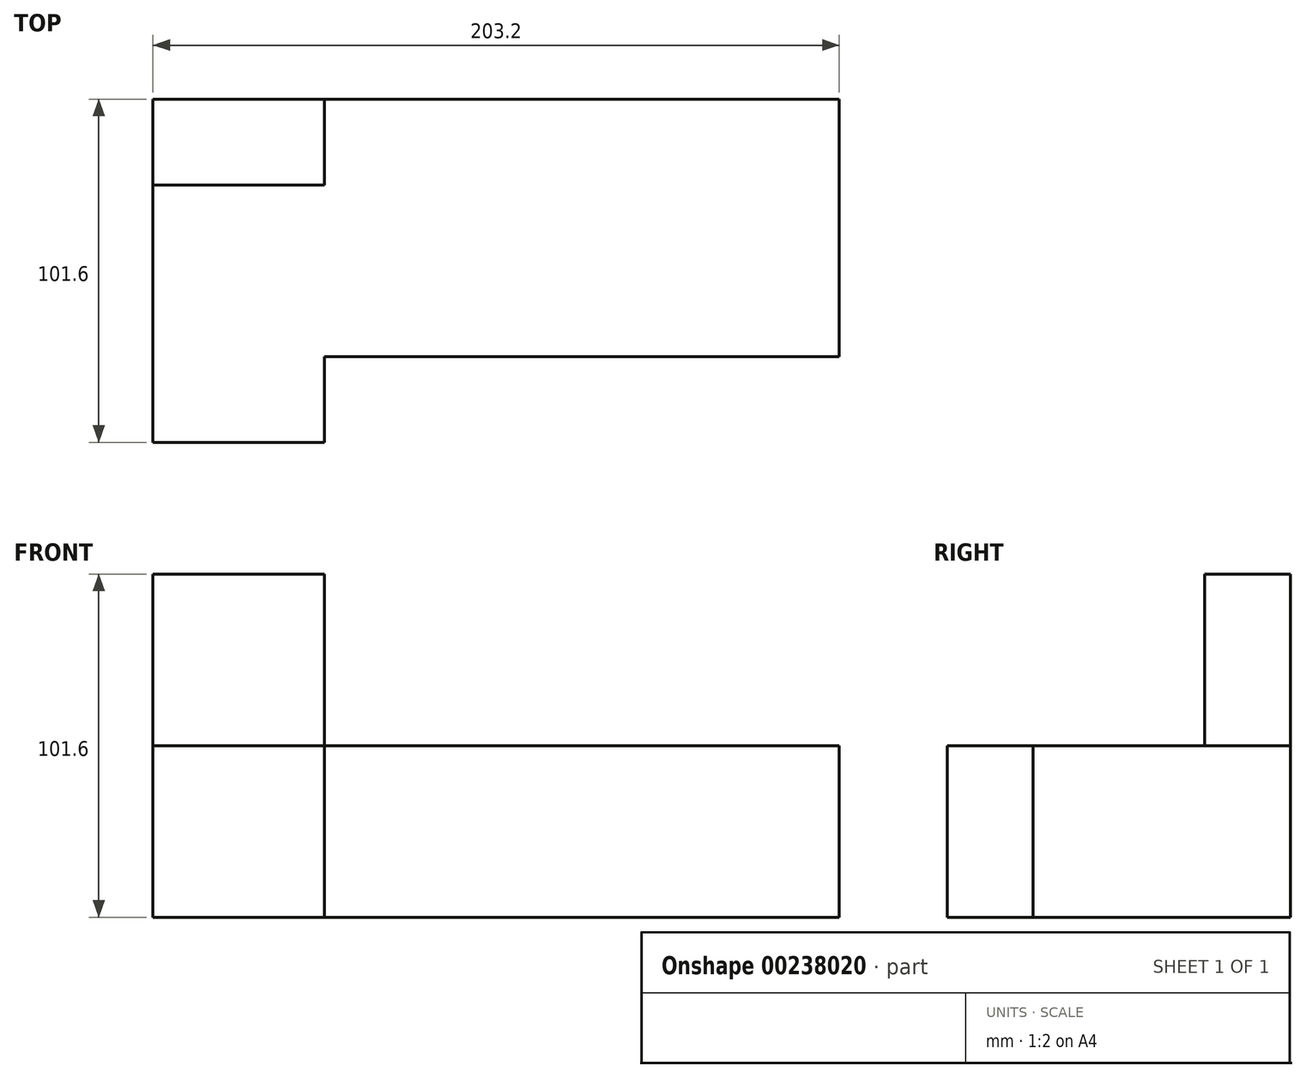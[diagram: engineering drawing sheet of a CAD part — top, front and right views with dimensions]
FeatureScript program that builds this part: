
annotation { "Feature Type Name" : "Feature", "Feature Type Description" : "" }
export const myFeature = defineFeature(function(context is Context, id is Id, definition is map)
    precondition{}
    {
        {
            var Q0;
            Q0=qCreatedBy(makeId("Front.planeOp"),FACE);
            var sketch = newSketch(context, id + "F0", { "sketchPlane" : qUnion([Q0])});
            skLineSegment(sketch, "E0.bottom", {"start": v(-128.64, 28.52) * mm, "end": v(74.56, 28.52) * mm});
            skLineSegment(sketch, "E0.top", {"start": v(-128.64, -22.28) * mm, "end": v(74.56, -22.28) * mm});
            skLineSegment(sketch, "E0.left", {"start": v(-128.64, 28.52) * mm, "end": v(-128.64, -22.28) * mm});
            skLineSegment(sketch, "E0.right", {"start": v(74.56, 28.52) * mm, "end": v(74.56, -22.28) * mm});
            skSolve(sketch);
        }
        {
            var Q0;
            Q0=makeQuery(id+"F0.imprint","IMPRINT",FACE,{"disambiguationData":[TD([[makeQuery(id+"F0.imprint","IMPRINT",EDGE,{"derivedFrom":sQuery(id+"F0.wireOp",EDGE,"E0.bottom")}),-1.0]])]});
            extrude(context, id + "F1", {"entities" : qUnion([Q0]), "depth" : 101.6 * mm});
        }
        {
            var Q0;
            Q0=makeQuery(id+"F1.opExtrude","CAP_FACE",FACE,{"disambiguationData":[OSD([sQuery(id+"F0.wireOp",EDGE,"E0.bottom"),sQuery(id+"F0.wireOp",EDGE,"E0.top"),sQuery(id+"F0.wireOp",EDGE,"E0.left"),sQuery(id+"F0.wireOp",EDGE,"E0.right")])],"isStart":false});
            var sketch = newSketch(context, id + "F2", { "sketchPlane" : qUnion([Q0])});
            skLineSegment(sketch, "E1.bottom", {"start": v(74.56, -22.28) * mm, "end": v(-77.84, -22.28) * mm});
            skLineSegment(sketch, "E1.top", {"start": v(74.56, 28.52) * mm, "end": v(-77.84, 28.52) * mm});
            skLineSegment(sketch, "E1.left", {"start": v(74.56, -22.28) * mm, "end": v(74.56, 28.52) * mm});
            skLineSegment(sketch, "E1.right", {"start": v(-77.84, -22.28) * mm, "end": v(-77.84, 28.52) * mm});
            skSolve(sketch);
        }
        {
            var Q0;
            Q0=makeQuery(id+"F2.imprint","IMPRINT",FACE,{"disambiguationData":[TD([[makeQuery(id+"F2.imprint","IMPRINT",EDGE,{"derivedFrom":sQuery(id+"F2.wireOp",EDGE,"E1.bottom")}),1.0]])]});
            extrude(context, id + "F3", {"entities" : qUnion([Q0]), "operationType" : NewBodyOperationType.REMOVE, "oppositeDirection" : true, "depth" : 25.4 * mm});
        }
        {
            var Q0;
            Q0=makeQuery(id+"F1.opExtrude","SWEPT_FACE",FACE,{"disambiguationData":[OSD([sQuery(id+"F0.wireOp",EDGE,"E0.bottom")])]});
            var sketch = newSketch(context, id + "F4", { "sketchPlane" : qUnion([Q0])});
            skLineSegment(sketch, "E2.bottom", {"start": v(-128.64, 0) * mm, "end": v(-77.84, 0) * mm});
            skLineSegment(sketch, "E2.top", {"start": v(-128.64, -25.4) * mm, "end": v(-77.84, -25.4) * mm});
            skLineSegment(sketch, "E2.left", {"start": v(-128.64, 0) * mm, "end": v(-128.64, -25.4) * mm});
            skLineSegment(sketch, "E2.right", {"start": v(-77.84, 0) * mm, "end": v(-77.84, -25.4) * mm});
            skSolve(sketch);
        }
        {
            var Q0;
            Q0=makeQuery(id+"F4.imprint","IMPRINT",FACE,{"disambiguationData":[TD([[makeQuery(id+"F4.imprint","IMPRINT",EDGE,{"derivedFrom":sQuery(id+"F4.wireOp",EDGE,"E2.bottom")}),-1.0]])]});
            extrude(context, id + "F5", {"entities" : qUnion([Q0]), "operationType" : NewBodyOperationType.ADD, "depth" : 50.8 * mm});
        }
    });
